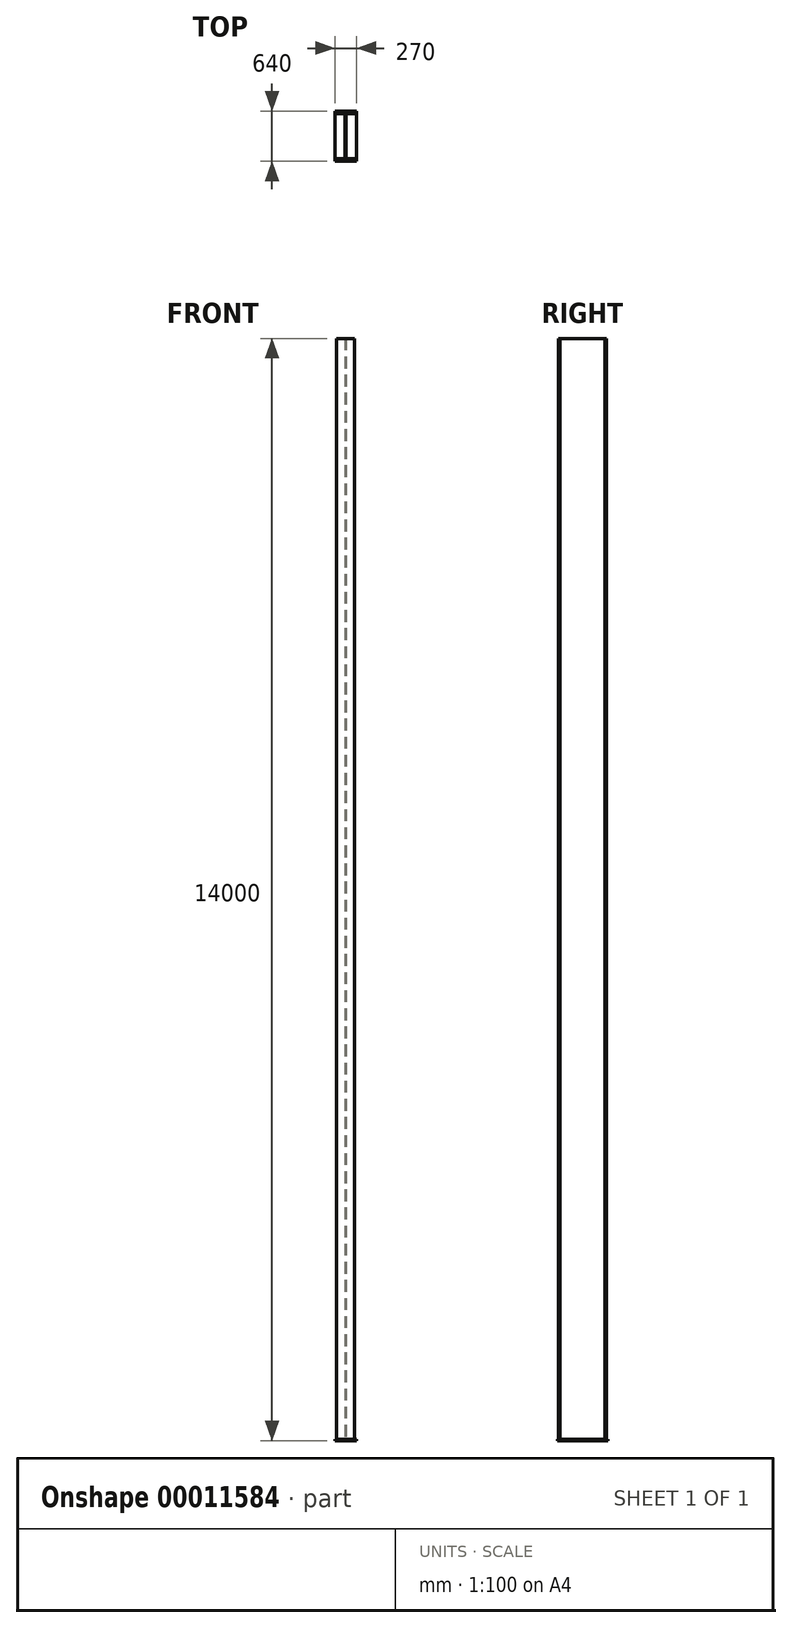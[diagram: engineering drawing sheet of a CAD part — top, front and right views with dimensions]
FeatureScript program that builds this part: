
annotation { "Feature Type Name" : "Feature", "Feature Type Description" : "" }
export const myFeature = defineFeature(function(context is Context, id is Id, definition is map)
    precondition{}
    {
        {
            var Q0;
            Q0=qCreatedBy(makeId("Top.planeOp"),FACE);
            var sketch = newSketch(context, id + "F0", { "sketchPlane" : qUnion([Q0])});
            skLineSegment(sketch, "E0.rect.bottom", {"start": v(114.5, 305) * mm, "end": v(-114.5, 305) * mm});
            skLineSegment(sketch, "E0.rect.top", {"start": v(114.5, -305) * mm, "end": v(-114.5, -305) * mm});
            skLineSegment(sketch, "E0.rect.left", {"start": v(114.5, 305) * mm, "end": v(114.5, 285.4) * mm});
            skLineSegment(sketch, "E0.rect.right", {"start": v(-114.5, 305) * mm, "end": v(-114.5, 285.4) * mm});
            skPoint(sketch, "E0.rect.middle", {"position": v(0, 0) * mm});
            skLineSegment(sketch, "E1.0", {"start": v(114.5, 285.4) * mm, "end": v(15.95, 285.4) * mm});
            skLineSegment(sketch, "E2.0", {"start": v(114.5, -285.4) * mm, "end": v(15.95, -285.4) * mm});
            skLineSegment(sketch, "E3.0", {"start": v(-5.95, 275.4) * mm, "end": v(-5.95, -275.4) * mm});
            skLineSegment(sketch, "E4.0", {"start": v(5.95, 275.4) * mm, "end": v(5.95, -275.4) * mm});
            skLineSegment(sketch, "E5.trimOffspring", {"start": v(-15.95, 285.4) * mm, "end": v(-114.5, 285.4) * mm});
            skLineSegment(sketch, "E6.trimOffspring", {"start": v(-15.95, -285.4) * mm, "end": v(-114.5, -285.4) * mm});
            skLineSegment(sketch, "E7.trimOffspring", {"start": v(-114.5, -285.4) * mm, "end": v(-114.5, -305) * mm});
            skLineSegment(sketch, "E8.trimOffspring", {"start": v(114.5, -285.4) * mm, "end": v(114.5, -305) * mm});
            skPoint(sketch, "E9.visualSharp", {"position": v(-5.95, -285.4) * mm});
            skArc(sketch, "E9.filletArc", {"start": v(-15.95, -285.4) * mm, "mid": v(-8.88, -282.47) * mm, "end": v(-5.95, -275.4) * mm});
            skPoint(sketch, "E10.visualSharp", {"position": v(5.95, -285.4) * mm});
            skArc(sketch, "E10.filletArc", {"start": v(5.95, -275.4) * mm, "mid": v(8.88, -282.47) * mm, "end": v(15.95, -285.4) * mm});
            skPoint(sketch, "E11.visualSharp", {"position": v(5.95, 285.4) * mm});
            skArc(sketch, "E11.filletArc", {"start": v(15.95, 285.4) * mm, "mid": v(8.88, 282.47) * mm, "end": v(5.95, 275.4) * mm});
            skPoint(sketch, "E12.visualSharp", {"position": v(-5.95, 285.4) * mm});
            skArc(sketch, "E12.filletArc", {"start": v(-5.95, 275.4) * mm, "mid": v(-8.88, 282.47) * mm, "end": v(-15.95, 285.4) * mm});
            skSolve(sketch);
        }
        {
            var Q0;
            Q0 = qSketchRegion(id + "F0", true);
            extrude(context, id + "F1", {"entities" : qUnion([Q0]), "depth" : 14000 * mm});
        }
        {
            var Q0;
            Q0=qCreatedBy(makeId("Top.planeOp"),FACE);
            var sketch = newSketch(context, id + "F2", { "sketchPlane" : qUnion([Q0])});
            skLineSegment(sketch, "E13.rect.bottom", {"start": v(135, 320) * mm, "end": v(-135, 320) * mm});
            skLineSegment(sketch, "E13.rect.top", {"start": v(135, -320) * mm, "end": v(-135, -320) * mm});
            skLineSegment(sketch, "E13.rect.left", {"start": v(135, 320) * mm, "end": v(135, -320) * mm});
            skLineSegment(sketch, "E13.rect.right", {"start": v(-135, 320) * mm, "end": v(-135, -320) * mm});
            skPoint(sketch, "E13.rect.middle", {"position": v(0, 0) * mm});
            skSolve(sketch);
        }
        {
            var Q0;
            Q0=makeQuery(id+"F2.imprint","IMPRINT",FACE,{"disambiguationData":[TD([[makeQuery(id+"F2.imprint","IMPRINT",EDGE,{"derivedFrom":sQuery(id+"F2.wireOp",EDGE,"E13.rect.bottom")}),1.0]])]});
            extrude(context, id + "F3", {"entities" : qUnion([Q0]), "operationType" : NewBodyOperationType.ADD, "depth" : 15 * mm});
        }
    });
